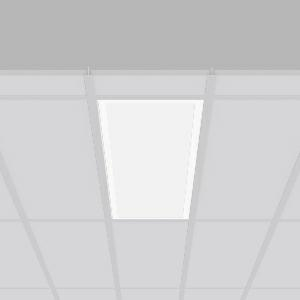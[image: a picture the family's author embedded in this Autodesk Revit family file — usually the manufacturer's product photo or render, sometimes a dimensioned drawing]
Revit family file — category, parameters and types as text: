
# Revit family: sidelite_eco_312367_002_790_cc39
name_source: partatom
category: Lighting Fixtures
units: mm (PartAtom-declared; Revit-internal decimal feet)

## family parameters
Cut with Voids When Loaded = No
Host = Face
Light Source = No
Part Type = Normal
Room Calculation Point = No
Round Connector Dimension = Use Diameter
Shared = No

## types (1)
- MultiLumen 1 (1 x LED Modul 830, 3200 lm, 3000)
    Apparent Load = 29 VA
    CIE Flux Codes = 47 79 96 100 100
    Color Rendering = 80
    Color Temperature = 3000
    Default Elevation = 1800 mm
    Description = Series: SIDELITE ECO
Highly economical recessed luminaire with progressive LED technology. Frame made of aluminium, powder-coated. Diffuser: plastic, opal. Lightguide and diffuser made of non-yellowing plastic (PMMA). Lateral light emission (RZB SIDELITE technology) for homogeneous light distribution. External driver. External driver with simple plug-in locking system and extended converter connecting cable to luminaire (1.90 m). MultiLumen: 4 steps adjustable luminous flux. Factory setting is the lowest offered step. Luminaire can be used with accessories (to be ordered separately) as recessed or surface mounting luminaire. Qualified for use in the food and drink industry. 
Colour: white
Length: 1245 mm
Width: 308 mm
Cut-out length: 1233 mm
Cut-out width: 296 mm
Recess height: 160 mm
Luminaire: recess height: 37 mm
Lamp: LED
Socket: without socket
Colour temperature: 3000K
Colour rendering index (CRI): 80
System power: 29 W
Rated luminous flux: 3200 lm
Luminous efficiency: 110 lm/W
System power 2: 33 W
Rated luminous flux 2: 3500 lm
Luminous efficiency 2: 106 lm/W
System power 3: 35 W
Rated luminous flux 3: 3700 lm
Luminous efficiency 3: 106 lm/W
System power 4: 38 W
Rated luminous flux 4: 4000 lm
Luminous efficiency 4: 105 lm/W
Control gear: Regulated power supply
Protection class: II
Type of protection: IP 40
    Height = 0 mm  [stored 0 ft]
    Lamp = 1 x LED Modul 830
    Lamp Light Flux = 3200 lm
    Lamp count = 1
    Length = 1245 mm
    Lifetime = 50000 h
    Luminous efficacy = 110 lm/W
    Manufacturer = RZB
    ModVariant = No
    Model = 312367.002.790
    Mounting Place = Ceiling
    Mounting Type = Recessed
    Number of Poles = 1
    OnlyDefault = Yes
    Power Factor = 1
    Product Name = SIDELITE ECO
    Product group = Recessed modular luminaires
    ProductGroupID = 406
    Protection Class = Protection class II
    Protection Degree = IP 20
    RLX_Detail_Level = 1
    RLX_Emergency_Light_Flux = 0 lm
    RLX_Emergency_Type = 0
    RLX_Emergency_Type_DB = No
    RlxData = <blob elided: 31537 chars, md5=fd51db2f>
    Socket = socket
    Standby Power = 0 W
    System Light Flux = 3200 lm
    System Power = 29 W
    Type Comments = MultiLumen 1
    Type Image = 312367.002.jpg
    URL = http://relux.com
    VarID = multilumen_1
    Voltage = 230 V
    Voltage Range = 220-240 V
    Weight = 0.00 kg
    Width = 308 mm

note: [stored X ft] marks values corroborated as IEEE doubles in the binary element streams (Revit-internal decimal feet)

## geometry (parser evidence)
native form markers: Blend x4, Sweep x9
no freeform markers — native parametric forms only
